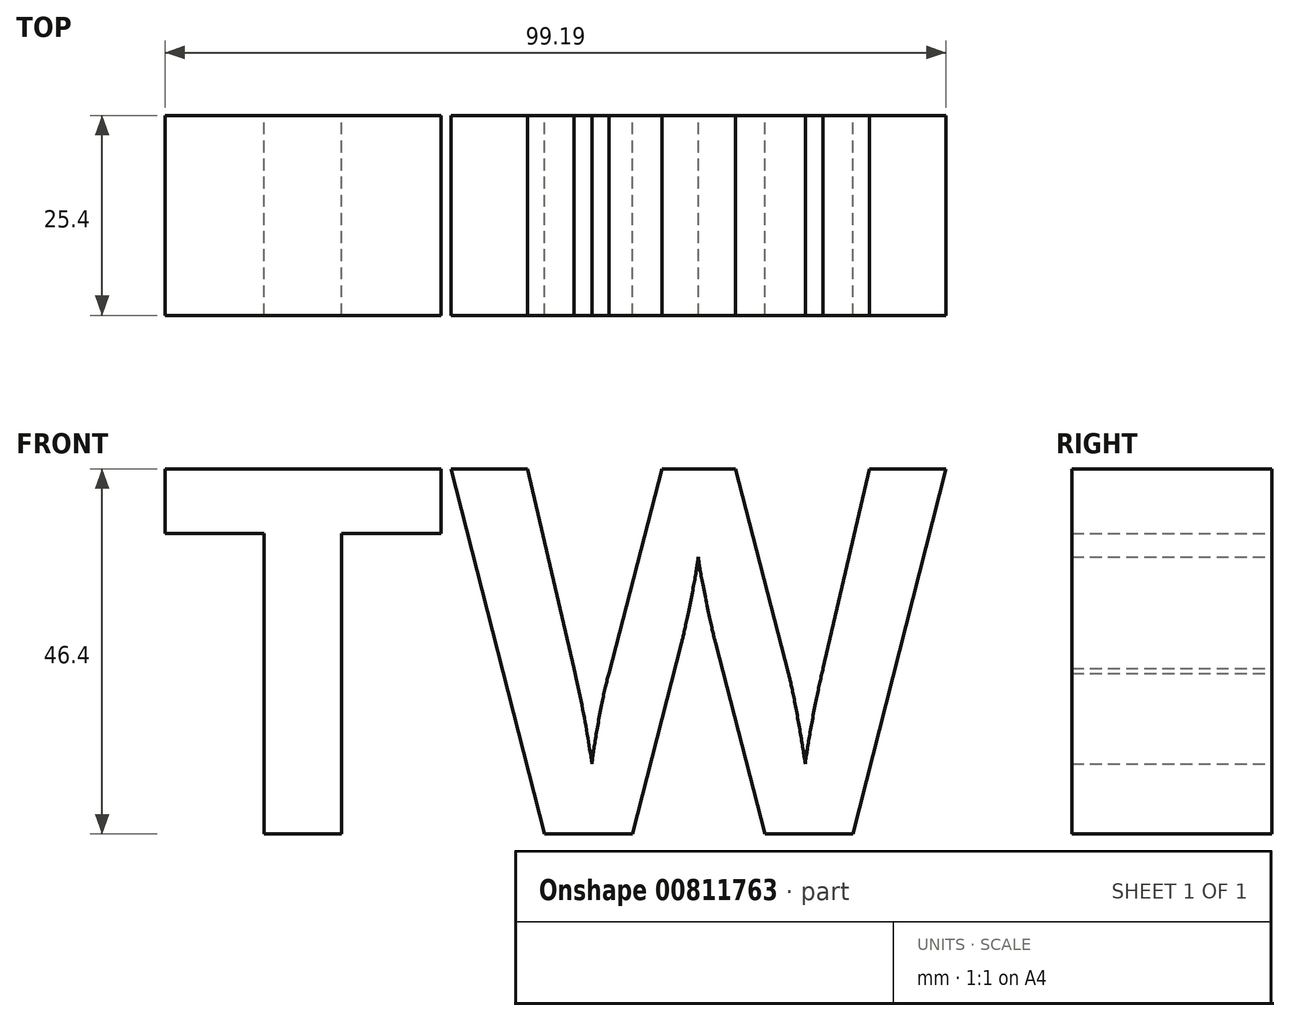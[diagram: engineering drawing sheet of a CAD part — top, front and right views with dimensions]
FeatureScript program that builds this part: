
annotation { "Feature Type Name" : "Feature", "Feature Type Description" : "" }
export const myFeature = defineFeature(function(context is Context, id is Id, definition is map)
    precondition{}
    {
        {
            var Q0;
            Q0=qCreatedBy(makeId("Front.planeOp"),FACE);
            var sketch = newSketch(context, id + "F0", { "sketchPlane" : qUnion([Q0])});
            skText(sketch, "E0", { "text": "TW", "fontName": "OpenSans-Bold.ttf"});
            const initialGuessF0  = {"E0": [-0.07538, 0.00445, 1, 0, 0.0468]};
            skSetInitialGuess(sketch, initialGuessF0);
            skSolve(sketch);
        }
        {
            var Q0;
            Q0=makeQuery(id+"F0.imprint","IMPRINT",FACE,{"disambiguationData":[TD([[makeQuery(id+"F0.imprint","IMPRINT",EDGE,{"derivedFrom":sQuery(id+"F0.wireOp",EDGE,"01959bff-7aa1-4a71-ad92-d4a0835bd2f1.sketch_text.stroke-0")}),-1.0]])]});
            var Q1;
            Q1=makeQuery(id+"F0.imprint","IMPRINT",FACE,{"disambiguationData":[TD([[makeQuery(id+"F0.imprint","IMPRINT",EDGE,{"derivedFrom":sQuery(id+"F0.wireOp",EDGE,"01959bff-7aa1-4a71-ad92-d4a0835bd2f1.sketch_text.stroke-8")}),-1.0]])]});
            var Q2;
            Q2=makeQuery(id+"F0.imprint","IMPRINT",FACE,{"disambiguationData":[TD([[makeQuery(id+"F0.imprint","IMPRINT",EDGE,{"derivedFrom":sQuery(id+"F0.wireOp",EDGE,"E0.sketch_text.stroke-0")}),-1.0]])]});
            var Q3;
            Q3=makeQuery(id+"F0.imprint","IMPRINT",FACE,{"disambiguationData":[TD([[makeQuery(id+"F0.imprint","IMPRINT",EDGE,{"derivedFrom":sQuery(id+"F0.wireOp",EDGE,"E0.sketch_text.stroke-8")}),-1.0]])]});
            extrude(context, id + "F1", {"entities" : qUnion([Q0, Q1, Q2, Q3]), "depth" : 25.4 * mm, "offsetDistance" : 25.4 * mm});
        }
    });
